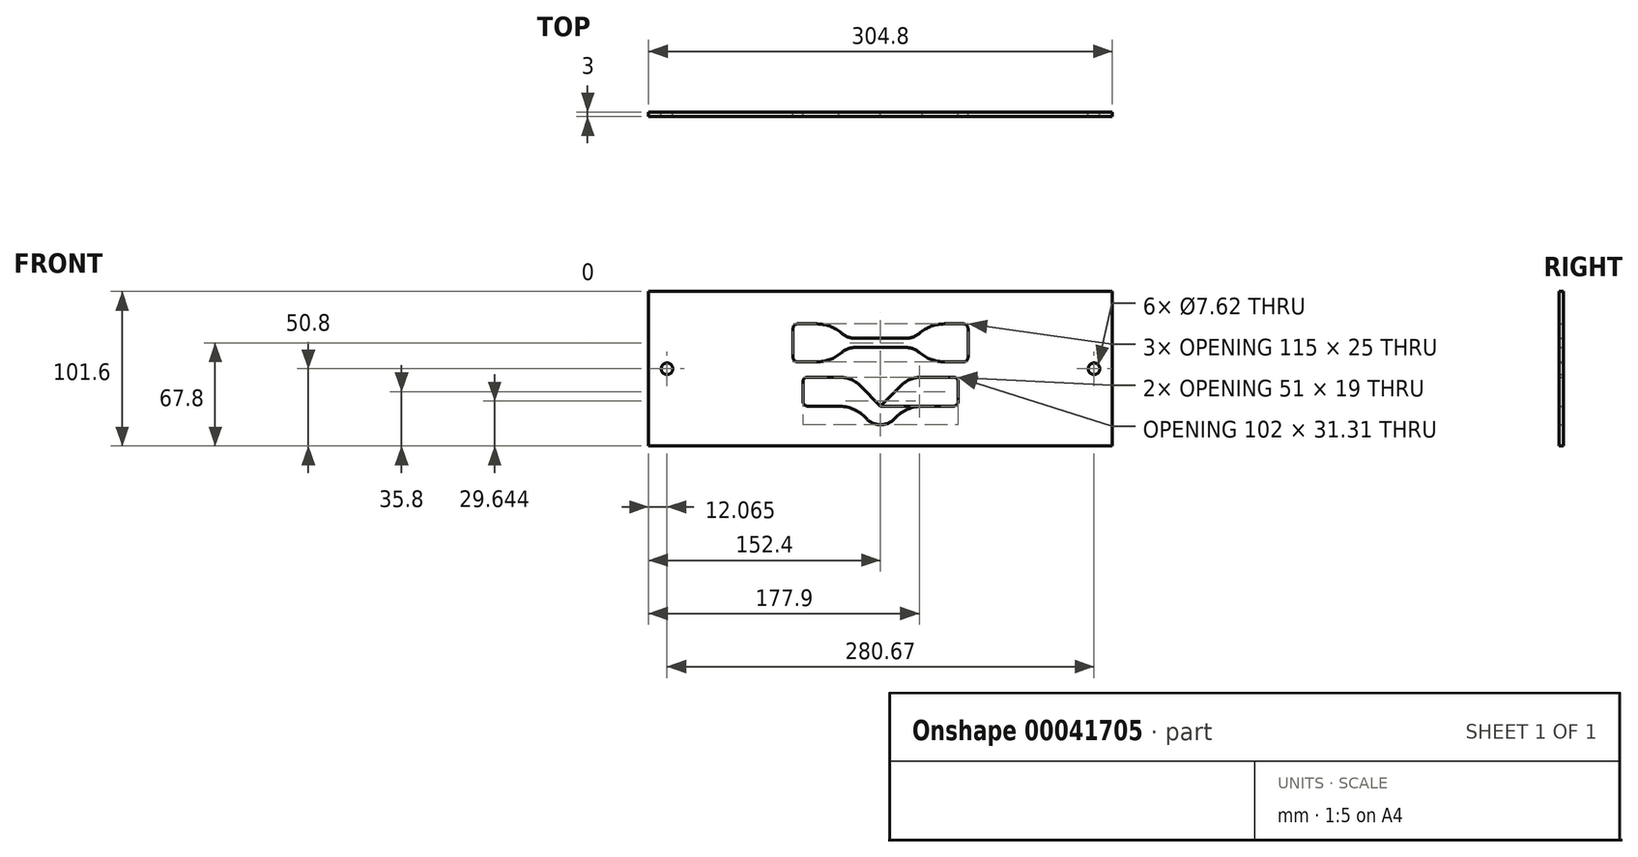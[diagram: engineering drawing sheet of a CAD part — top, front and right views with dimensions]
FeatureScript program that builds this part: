
annotation { "Feature Type Name" : "Feature", "Feature Type Description" : "" }
export const myFeature = defineFeature(function(context is Context, id is Id, definition is map)
    precondition{}
    {
        {
            var Q0;
            Q0=qCreatedBy(makeId("Front.planeOp"),FACE);
            var sketch = newSketch(context, id + "F0", { "sketchPlane" : qUnion([Q0])});
            skLineSegment(sketch, "E0", {"start": v(-57.5, 0) * mm, "end": v(-57.5, 9.5) * mm});
            skLineSegment(sketch, "E1", {"start": v(-54.5, 12.5) * mm, "end": v(-42, 12.5) * mm});
            skLineSegment(sketch, "E2", {"start": v(-16.5, 3) * mm, "end": v(0, 3) * mm});
            skLineSegment(sketch, "E3", {"start": v(-25.66, 6.41) * mm, "end": v(-25.66, 6.41) * mm});
            skPoint(sketch, "E4.visualSharp", {"position": v(-21.71, 3) * mm});
            skArc(sketch, "E4.filletArc", {"start": v(-25.66, 6.41) * mm, "mid": v(-21.39, 3.88) * mm, "end": v(-16.5, 3) * mm});
            skPoint(sketch, "E5.visualSharp", {"position": v(-32.7, 12.5) * mm});
            skArc(sketch, "E5.filletArc", {"start": v(-25.66, 6.41) * mm, "mid": v(-33.29, 10.93) * mm, "end": v(-42, 12.5) * mm});
            skArc(sketch, "E6.MirrorCS", {"start": v(25.66, 6.41) * mm, "mid": v(21.39, 3.88) * mm, "end": v(16.5, 3) * mm});
            skLineSegment(sketch, "E7.MirrorCS", {"start": v(57.5, 0) * mm, "end": v(57.5, 9.5) * mm});
            skLineSegment(sketch, "E8.MirrorCS", {"start": v(54.5, 12.5) * mm, "end": v(42, 12.5) * mm});
            skLineSegment(sketch, "E9.MirrorCS", {"start": v(16.5, 3) * mm, "end": v(0, 3) * mm});
            skLineSegment(sketch, "E10.MirrorCS", {"start": v(25.66, 6.41) * mm, "end": v(25.66, 6.41) * mm});
            skArc(sketch, "E11.MirrorCS", {"start": v(25.66, 6.41) * mm, "mid": v(33.29, 10.93) * mm, "end": v(42, 12.5) * mm});
            skPoint(sketch, "E12.MirrorP", {"position": v(32.7, 12.5) * mm});
            skPoint(sketch, "E13.MirrorP", {"position": v(21.71, 3) * mm});
            skArc(sketch, "E14.MirrorCS", {"start": v(25.66, -6.41) * mm, "mid": v(21.39, -3.88) * mm, "end": v(16.5, -3) * mm});
            skArc(sketch, "E15.MirrorCS", {"start": v(-25.66, -6.41) * mm, "mid": v(-21.39, -3.88) * mm, "end": v(-16.5, -3) * mm});
            skPoint(sketch, "E16.MirrorP", {"position": v(32.7, -12.5) * mm});
            skPoint(sketch, "E17.MirrorP", {"position": v(21.71, -3) * mm});
            skLineSegment(sketch, "E18.MirrorCS", {"start": v(-25.66, -6.41) * mm, "end": v(-25.66, -6.41) * mm});
            skArc(sketch, "E19.MirrorCS", {"start": v(25.66, -6.41) * mm, "mid": v(33.29, -10.93) * mm, "end": v(42, -12.5) * mm});
            skLineSegment(sketch, "E20.MirrorCS", {"start": v(16.5, -3) * mm, "end": v(0, -3) * mm});
            skLineSegment(sketch, "E21.MirrorCS", {"start": v(54.5, -12.5) * mm, "end": v(42, -12.5) * mm});
            skArc(sketch, "E22.MirrorCS", {"start": v(-25.66, -6.41) * mm, "mid": v(-33.29, -10.93) * mm, "end": v(-42, -12.5) * mm});
            skLineSegment(sketch, "E23.MirrorCS", {"start": v(-54.5, -12.5) * mm, "end": v(-42, -12.5) * mm});
            skPoint(sketch, "E24.MirrorP", {"position": v(-32.7, -12.5) * mm});
            skLineSegment(sketch, "E25.MirrorCS", {"start": v(-57.5, 0) * mm, "end": v(-57.5, -9.5) * mm});
            skPoint(sketch, "E26.MirrorP", {"position": v(-21.71, -3) * mm});
            skLineSegment(sketch, "E27.MirrorCS", {"start": v(-16.5, -3) * mm, "end": v(0, -3) * mm});
            skLineSegment(sketch, "E28.MirrorCS", {"start": v(57.5, 0) * mm, "end": v(57.5, -9.5) * mm});
            skLineSegment(sketch, "E29.MirrorCS", {"start": v(25.66, -6.41) * mm, "end": v(25.66, -6.41) * mm});
            skPoint(sketch, "E30.visualSharp", {"position": v(-57.5, 12.5) * mm});
            skArc(sketch, "E30.filletArc", {"start": v(-54.5, 12.5) * mm, "mid": v(-56.62, 11.62) * mm, "end": v(-57.5, 9.5) * mm});
            skPoint(sketch, "E31.visualSharp", {"position": v(-57.5, -12.5) * mm});
            skArc(sketch, "E31.filletArc", {"start": v(-57.5, -9.5) * mm, "mid": v(-56.62, -11.62) * mm, "end": v(-54.5, -12.5) * mm});
            skPoint(sketch, "E32.visualSharp", {"position": v(57.5, 12.5) * mm});
            skArc(sketch, "E32.filletArc", {"start": v(57.5, 9.5) * mm, "mid": v(56.62, 11.62) * mm, "end": v(54.5, 12.5) * mm});
            skPoint(sketch, "E33.visualSharp", {"position": v(57.5, -12.5) * mm});
            skArc(sketch, "E33.filletArc", {"start": v(54.5, -12.5) * mm, "mid": v(56.62, -11.62) * mm, "end": v(57.5, -9.5) * mm});
            skLineSegment(sketch, "E34", {"start": v(-51, -25.5) * mm, "end": v(-51, -38.5) * mm});
            skLineSegment(sketch, "E35", {"start": v(-48, -22.5) * mm, "end": v(-27.34, -22.5) * mm});
            skLineSegment(sketch, "E36", {"start": v(-13.44, -28.06) * mm, "end": v(0, -41.5) * mm});
            skLineSegment(sketch, "E37", {"start": v(-48, -41.5) * mm, "end": v(-27.87, -41.5) * mm});
            skLineSegment(sketch, "E38", {"start": v(0, -41.5) * mm, "end": v(0, -87.73) * mm, "construction": true});
            skPoint(sketch, "E39.visualSharp", {"position": v(-19, -22.5) * mm});
            skLineSegment(sketch, "E40", {"start": v(-27.87, -41.5) * mm, "end": v(0, -41.5) * mm, "construction": true});
            skArc(sketch, "E41", {"start": v(-9.39, -49.66) * mm, "mid": v(-17.77, -43.63) * mm, "end": v(-27.87, -41.5) * mm});
            skLineSegment(sketch, "E42", {"start": v(-9.39, -49.66) * mm, "end": v(-9.39, -49.66) * mm});
            skArc(sketch, "E43.MirrorCS", {"start": v(13.44, -28.06) * mm, "mid": v(19.82, -23.85) * mm, "end": v(27.34, -22.5) * mm});
            skLineSegment(sketch, "E44.MirrorCS", {"start": v(13.44, -28.06) * mm, "end": v(0, -41.5) * mm});
            skLineSegment(sketch, "E45.MirrorCS", {"start": v(48, -22.5) * mm, "end": v(27.34, -22.5) * mm});
            skPoint(sketch, "E46.MirrorP", {"position": v(19, -22.5) * mm});
            skLineSegment(sketch, "E47.MirrorCS", {"start": v(48, -41.5) * mm, "end": v(27.87, -41.5) * mm});
            skLineSegment(sketch, "E48.MirrorCS", {"start": v(9.39, -49.66) * mm, "end": v(9.39, -49.66) * mm});
            skLineSegment(sketch, "E49.MirrorCS", {"start": v(51, -25.5) * mm, "end": v(51, -38.5) * mm});
            skArc(sketch, "E50.MirrorCS", {"start": v(9.39, -49.66) * mm, "mid": v(17.77, -43.63) * mm, "end": v(27.87, -41.5) * mm});
            skLineSegment(sketch, "E51.MirrorCS", {"start": v(27.87, -41.5) * mm, "end": v(0, -41.5) * mm});
            skPoint(sketch, "E52.visualSharp", {"position": v(0, -59.97) * mm});
            skArc(sketch, "E52.filletArc", {"start": v(-9.39, -49.66) * mm, "mid": v(0, -53.81) * mm, "end": v(9.39, -49.66) * mm});
            skArc(sketch, "E53.trimOffspring", {"start": v(-13.44, -28.06) * mm, "mid": v(-19.82, -23.85) * mm, "end": v(-27.34, -22.5) * mm});
            skPoint(sketch, "E54.center.orphan", {"position": v(-26.87, -41.5) * mm});
            skLineSegment(sketch, "E55", {"start": v(0, 3) * mm, "end": v(0, -41.11) * mm, "construction": true});
            skPoint(sketch, "E56.visualSharp", {"position": v(-51, -22.5) * mm});
            skArc(sketch, "E56.filletArc", {"start": v(-48, -22.5) * mm, "mid": v(-50.12, -23.38) * mm, "end": v(-51, -25.5) * mm});
            skPoint(sketch, "E57.visualSharp", {"position": v(-51, -41.5) * mm});
            skArc(sketch, "E57.filletArc", {"start": v(-51, -38.5) * mm, "mid": v(-50.12, -40.62) * mm, "end": v(-48, -41.5) * mm});
            skPoint(sketch, "E58.visualSharp", {"position": v(51, -22.5) * mm});
            skArc(sketch, "E58.filletArc", {"start": v(51, -25.5) * mm, "mid": v(50.12, -23.38) * mm, "end": v(48, -22.5) * mm});
            skPoint(sketch, "E59.visualSharp", {"position": v(51, -41.5) * mm});
            skArc(sketch, "E59.filletArc", {"start": v(48, -41.5) * mm, "mid": v(50.12, -40.62) * mm, "end": v(51, -38.5) * mm});
            skLineSegment(sketch, "E60", {"start": v(0, -17) * mm, "end": v(-136.53, -17) * mm, "construction": true});
            skPoint(sketch, "E60.startSnap0", {"position": v(0, -19.06) * mm});
            skCircle(sketch, "E61", {"center": v(-140.34, -17) * mm, "radius": 3.81 * mm});
            skCircle(sketch, "E62.MirrorC", {"center": v(140.34, -17) * mm, "radius": 3.81 * mm});
            skLineSegment(sketch, "E63.rect.bottom", {"start": v(-152.4, 33.8) * mm, "end": v(152.4, 33.8) * mm});
            skLineSegment(sketch, "E63.rect.top", {"start": v(-152.4, -67.8) * mm, "end": v(152.4, -67.8) * mm});
            skLineSegment(sketch, "E63.rect.left", {"start": v(-152.4, 33.8) * mm, "end": v(-152.4, -67.8) * mm});
            skLineSegment(sketch, "E63.rect.right", {"start": v(152.4, 33.8) * mm, "end": v(152.4, -67.8) * mm});
            skPoint(sketch, "E63.rect.middle", {"position": v(0, -17) * mm});
            skSolve(sketch);
        }
        {
            var Q0;
            Q0=makeQuery(id+"F0.imprint","IMPRINT",FACE,{"disambiguationData":[TD([[makeQuery(id+"F0.imprint","IMPRINT",EDGE,{"derivedFrom":sQuery(id+"F0.wireOp",EDGE,"E34")}),1.0]])]});
            var Q1;
            Q1=makeQuery(id+"F0.imprint","IMPRINT",FACE,{"disambiguationData":[TD([[makeQuery(id+"F0.imprint","IMPRINT",EDGE,{"derivedFrom":sQuery(id+"F0.wireOp",EDGE,"E43.MirrorCS")}),-1.0]])]});
            extrude(context, id + "F1", {"entities" : qUnion([Q0, Q1]), "depth" : 3 * mm});
        }
        {
            var Q0;
            Q0 = qSketchRegion(id + "F0", true);
            extrude(context, id + "F2", {"entities" : qUnion([Q0]), "depth" : 3 * mm});
        }
        {
            var Q0;
            Q0=makeQuery(id+"F0.imprint","IMPRINT",FACE,{"disambiguationData":[TD([[makeQuery(id+"F0.imprint","IMPRINT",EDGE,{"derivedFrom":sQuery(id+"F0.wireOp",EDGE,"E0")}),-1.0]])]});
            extrude(context, id + "F3", {"entities" : qUnion([Q0]), "depth" : 3 * mm});
        }
        {
            var Q0;
            Q0=makeQuery(id+"F0.imprint","IMPRINT",FACE,{"disambiguationData":[TD([[makeQuery(id+"F0.imprint","IMPRINT",EDGE,{"derivedFrom":sQuery(id+"F0.wireOp",EDGE,"E43.MirrorCS")}),-1.0]])]});
            var Q1;
            Q1=makeQuery(id+"F0.imprint","IMPRINT",FACE,{"disambiguationData":[TD([[makeQuery(id+"F0.imprint","IMPRINT",EDGE,{"derivedFrom":sQuery(id+"F0.wireOp",EDGE,"E34")}),1.0]])]});
            extrude(context, id + "F4", {"entities" : qUnion([Q0, Q1]), "depth" : 3 * mm});
        }
    });
